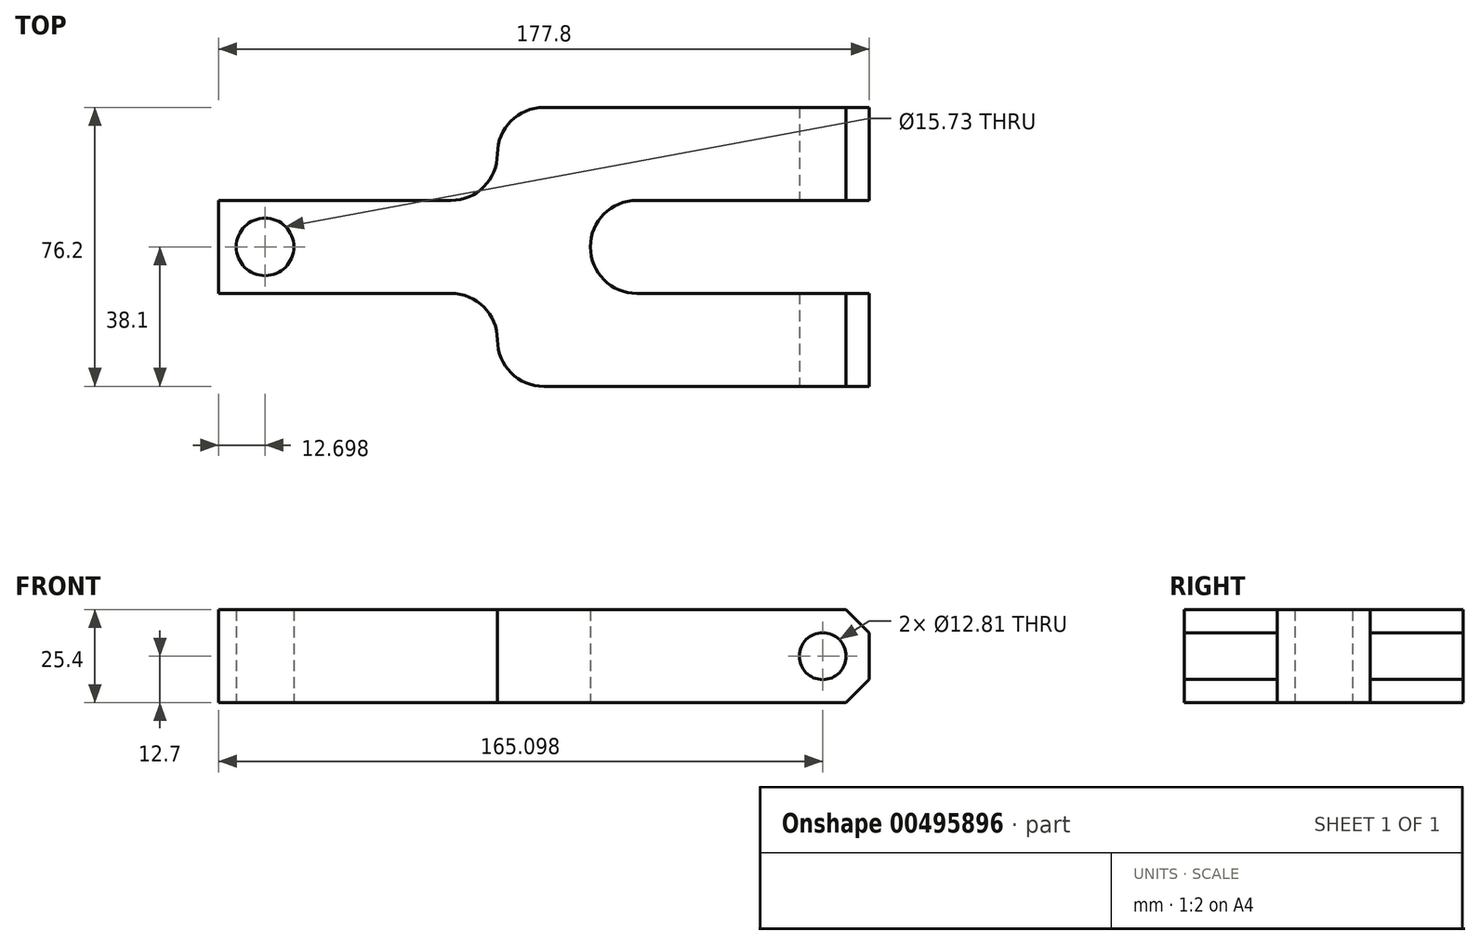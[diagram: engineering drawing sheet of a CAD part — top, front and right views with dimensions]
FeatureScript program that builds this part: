
annotation { "Feature Type Name" : "Feature", "Feature Type Description" : "" }
export const myFeature = defineFeature(function(context is Context, id is Id, definition is map)
    precondition{}
    {
        {
            var Q0;
            Q0=qCreatedBy(makeId("Top.planeOp"),FACE);
            var sketch = newSketch(context, id + "F0", { "sketchPlane" : qUnion([Q0])});
            skLineSegment(sketch, "E0.bottom", {"start": v(-19.2, -12.7) * mm, "end": v(-82.7, -12.7) * mm});
            skLineSegment(sketch, "E0.top", {"start": v(-19.2, 12.7) * mm, "end": v(-82.7, 12.7) * mm});
            skLineSegment(sketch, "E0.left", {"start": v(18.9, 0) * mm, "end": v(18.9, 0) * mm});
            skLineSegment(sketch, "E0.right", {"start": v(-82.7, -12.7) * mm, "end": v(-82.7, 12.7) * mm});
            skPoint(sketch, "E0.middle", {"position": v(-31.9, 0) * mm});
            skLineSegment(sketch, "E1.bottom", {"start": v(95.1, 12.7) * mm, "end": v(31.6, 12.7) * mm});
            skLineSegment(sketch, "E1.top", {"start": v(95.1, 38.1) * mm, "end": v(6.2, 38.1) * mm});
            skLineSegment(sketch, "E1.left", {"start": v(95.1, 12.7) * mm, "end": v(95.1, 38.1) * mm});
            skLineSegment(sketch, "E1.right", {"start": v(-6.5, 25.4) * mm, "end": v(-6.5, 25.4) * mm});
            skPoint(sketch, "E1.middle", {"position": v(44.3, 25.4) * mm});
            skLineSegment(sketch, "E2.bottom", {"start": v(95.1, -38.1) * mm, "end": v(6.2, -38.1) * mm});
            skLineSegment(sketch, "E2.top", {"start": v(95.1, -12.7) * mm, "end": v(31.6, -12.7) * mm});
            skLineSegment(sketch, "E2.left", {"start": v(95.1, -38.1) * mm, "end": v(95.1, -12.7) * mm});
            skLineSegment(sketch, "E2.right", {"start": v(-6.5, -25.4) * mm, "end": v(-6.5, -25.4) * mm});
            skPoint(sketch, "E2.middle", {"position": v(44.3, -25.4) * mm});
            skPoint(sketch, "E3.newPointA", {"position": v(-6.5, 12.7) * mm});
            skPoint(sketch, "E3.newPointB", {"position": v(18.9, 12.7) * mm});
            skArc(sketch, "E3.filletArc", {"start": v(31.6, 12.7) * mm, "mid": v(22.62, 8.98) * mm, "end": v(18.9, 0) * mm});
            skPoint(sketch, "E4.newPointB", {"position": v(-6.5, -12.7) * mm});
            skArc(sketch, "E4.filletArc", {"start": v(18.9, 0) * mm, "mid": v(22.62, -8.98) * mm, "end": v(31.6, -12.7) * mm});
            skArc(sketch, "E5.filletArc", {"start": v(-19.2, 12.7) * mm, "mid": v(-10.22, 16.42) * mm, "end": v(-6.5, 25.4) * mm});
            skPoint(sketch, "E6.visualSharp", {"position": v(-6.5, 38.1) * mm});
            skArc(sketch, "E6.filletArc", {"start": v(6.2, 38.1) * mm, "mid": v(-2.78, 34.38) * mm, "end": v(-6.5, 25.4) * mm});
            skPoint(sketch, "E7.newPointA", {"position": v(18.9, -12.7) * mm});
            skArc(sketch, "E7.filletArc", {"start": v(-6.5, -25.4) * mm, "mid": v(-10.22, -16.42) * mm, "end": v(-19.2, -12.7) * mm});
            skPoint(sketch, "E8.visualSharp", {"position": v(-6.5, -38.1) * mm});
            skArc(sketch, "E8.filletArc", {"start": v(-6.5, -25.4) * mm, "mid": v(-2.78, -34.38) * mm, "end": v(6.2, -38.1) * mm});
            skCircle(sketch, "E9", {"center": v(-70, 0) * mm, "radius": 7.87 * mm});
            skSolve(sketch);
        }
        {
            var Q0;
            Q0 = qSketchRegion(id + "F0", true);
            extrude(context, id + "F1", {"entities" : qUnion([Q0]), "endBound" : BoundingType.SYMMETRIC, "depth" : 25.4 * mm});
        }
        {
            var Q0;
            Q0=qCreatedBy(makeId("Front.planeOp"),FACE);
            var sketch = newSketch(context, id + "F2", { "sketchPlane" : qUnion([Q0])});
            skCircle(sketch, "E10", {"center": v(82.4, 0) * mm, "radius": 6.4 * mm});
            skSolve(sketch);
        }
        {
            var Q0;
            Q0 = qSketchRegion(id + "F2", true);
            extrude(context, id + "F3", {"entities" : qUnion([Q0]), "operationType" : NewBodyOperationType.REMOVE, "endBound" : BoundingType.SYMMETRIC, "oppositeDirection" : true, "depth" : 88.9 * mm});
        }
        {
            var Q0;
            Q0=makeQuery(id+"F1.opExtrude","CAP_EDGE",EDGE,{"disambiguationData":[OSD([sQuery(id+"F0.wireOp",EDGE,"E2.left")])],"isStart":false});
            var Q1;
            Q1=makeQuery(id+"F1.opExtrude","CAP_EDGE",EDGE,{"disambiguationData":[OSD([sQuery(id+"F0.wireOp",EDGE,"E2.left")])],"isStart":true});
            chamfer(context, id + "F4", {"entities" : qUnion([Q0, Q1]), "width" : 6.35 * mm, "tangentPropagation" : true});
        }
        {
            var Q0;
            Q0=makeQuery(id+"F1.opExtrude","CAP_EDGE",EDGE,{"disambiguationData":[OSD([sQuery(id+"F0.wireOp",EDGE,"E1.left")])],"isStart":false});
            var Q1;
            Q1=makeQuery(id+"F1.opExtrude","CAP_EDGE",EDGE,{"disambiguationData":[OSD([sQuery(id+"F0.wireOp",EDGE,"E1.left")])],"isStart":true});
            chamfer(context, id + "F5", {"entities" : qUnion([Q0, Q1]), "width" : 6.35 * mm, "tangentPropagation" : true});
        }
    });
